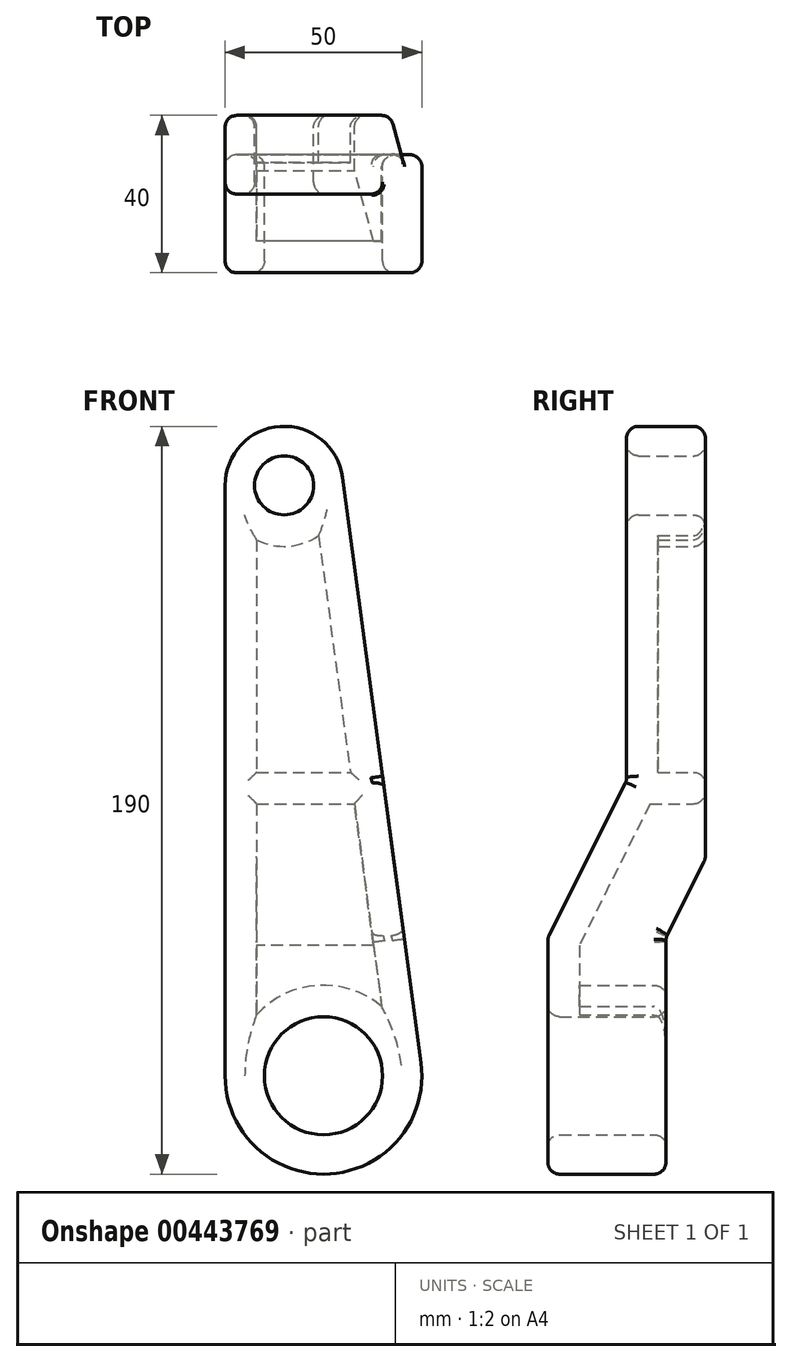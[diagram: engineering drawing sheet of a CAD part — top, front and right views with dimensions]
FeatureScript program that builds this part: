
annotation { "Feature Type Name" : "Feature", "Feature Type Description" : "" }
export const myFeature = defineFeature(function(context is Context, id is Id, definition is map)
    precondition{}
    {
        {
            var Q0;
            Q0=qCreatedBy(makeId("Front.planeOp"),FACE);
            var sketch = newSketch(context, id + "F0", { "sketchPlane" : qUnion([Q0])});
            skArc(sketch, "E0", {"start": v(-25, 0) * mm, "mid": v(1.66, -24.94) * mm, "end": v(24.78, 3.32) * mm});
            skArc(sketch, "E1", {"start": v(4.87, 152) * mm, "mid": v(-11, 164.97) * mm, "end": v(-25, 150) * mm});
            skLineSegment(sketch, "E2", {"start": v(-25, 150) * mm, "end": v(-25, 0) * mm});
            skLineSegment(sketch, "E3", {"start": v(4.87, 152) * mm, "end": v(24.78, 3.32) * mm});
            skPoint(sketch, "E4.orphan", {"position": v(0, 188.33) * mm});
            skSolve(sketch);
        }
        {
            var Q0;
            Q0=makeQuery(id+"F0.imprint","IMPRINT",FACE,{"disambiguationData":[TD([[makeQuery(id+"F0.imprint","IMPRINT",EDGE,{"derivedFrom":sQuery(id+"F0.wireOp",EDGE,"E0")}),1.0]])]});
            extrude(context, id + "F1", {"entities" : qUnion([Q0]), "depth" : 40 * mm});
        }
        {
            var Q0;
            Q0=makeQuery(id+"F1.opExtrude","SWEPT_FACE",FACE,{"disambiguationData":[OSD([sQuery(id+"F0.wireOp",EDGE,"E2")])]});
            var sketch = newSketch(context, id + "F2", { "sketchPlane" : qUnion([Q0])});
            skPoint(sketch, "E5.endSnap0", {"position": v(20, 0) * mm});
            skLineSegment(sketch, "E6", {"start": v(0, 55) * mm, "end": v(0, -25.94) * mm});
            skLineSegment(sketch, "E7", {"start": v(10, -25.94) * mm, "end": v(10, 35) * mm});
            skLineSegment(sketch, "E8", {"start": v(10, 35) * mm, "end": v(0, 55) * mm});
            skLineSegment(sketch, "E9", {"start": v(40, 35) * mm, "end": v(40, 165.97) * mm});
            skLineSegment(sketch, "E10", {"start": v(20, 165.97) * mm, "end": v(20, 75) * mm});
            skLineSegment(sketch, "E11", {"start": v(20, 75) * mm, "end": v(40, 35) * mm});
            skLineSegment(sketch, "E12", {"start": v(0, -25.94) * mm, "end": v(10, -25.94) * mm});
            skLineSegment(sketch, "E13", {"start": v(20, 165.97) * mm, "end": v(40, 165.97) * mm});
            skSolve(sketch);
        }
        {
            var Q0;
            Q0 = qSketchRegion(id + "F2", true);
            extrude(context, id + "F3", {"entities" : qUnion([Q0]), "operationType" : NewBodyOperationType.REMOVE, "endBound" : BoundingType.THROUGH_ALL, "oppositeDirection" : true, "depth" : 25 * mm});
        }
        {
            var Q0;
            Q0=makeQuery(id+"F1.opExtrude","CAP_FACE",FACE,{"disambiguationData":[OSD([sQuery(id+"F0.wireOp",EDGE,"E0"),sQuery(id+"F0.wireOp",EDGE,"E1"),sQuery(id+"F0.wireOp",EDGE,"E2"),sQuery(id+"F0.wireOp",EDGE,"E3")])],"isStart":true});
            var sketch = newSketch(context, id + "F4", { "sketchPlane" : qUnion([Q0])});
            skCircle(sketch, "E14", {"center": v(10, 150) * mm, "radius": 7.5 * mm});
            skCircle(sketch, "E15", {"center": v(0, 0) * mm, "radius": 15 * mm});
            skSolve(sketch);
        }
        {
            var Q0;
            Q0 = qSketchRegion(id + "F4", true);
            extrude(context, id + "F5", {"entities" : qUnion([Q0]), "operationType" : NewBodyOperationType.REMOVE, "endBound" : BoundingType.THROUGH_ALL, "oppositeDirection" : true, "depth" : 25 * mm});
        }
        {
            var Q0;
            Q0=makeQuery(id+"F1.opExtrude","CAP_FACE",FACE,{"disambiguationData":[OSD([sQuery(id+"F0.wireOp",EDGE,"E0"),sQuery(id+"F0.wireOp",EDGE,"E1"),sQuery(id+"F0.wireOp",EDGE,"E2"),sQuery(id+"F0.wireOp",EDGE,"E3")])],"isStart":true});
            var Q1;
            Q1=makeQuery(id+"F3.boolean.opBoolean","COPY",FACE,{"derivedFrom":makeQuery(id+"F3.opExtrude","SWEPT_FACE",FACE,{"disambiguationData":[OSD([sQuery(id+"F2.wireOp",EDGE,"E8")])]})});
            var Q2;
            Q2=makeQuery(id+"F3.boolean.opBoolean","COPY",FACE,{"derivedFrom":makeQuery(id+"F3.opExtrude","SWEPT_FACE",FACE,{"disambiguationData":[OSD([sQuery(id+"F2.wireOp",EDGE,"E7")])]})});
            shell(context, id + "F6", {"entities" : qUnion([Q0, Q1, Q2]), "thickness" : 8 * mm});
        }
        {
            var Q0;
            Q0=makeQuery(id+"F1.opExtrude","CAP_FACE",FACE,{"disambiguationData":[OSD([sQuery(id+"F0.wireOp",EDGE,"E0"),sQuery(id+"F0.wireOp",EDGE,"E1"),sQuery(id+"F0.wireOp",EDGE,"E2"),sQuery(id+"F0.wireOp",EDGE,"E3")])],"isStart":true});
            var sketch = newSketch(context, id + "F7", { "sketchPlane" : qUnion([Q0])});
            skLineSegment(sketch, "E16", {"start": v(-6.82, 77.11) * mm, "end": v(17, 77.11) * mm});
            skLineSegment(sketch, "E17", {"start": v(-7.9, 69.11) * mm, "end": v(17, 69.11) * mm});
            skLineSegment(sketch, "E18.0", {"start": v(-6.82, 77.11) * mm, "end": v(-7.9, 69.11) * mm});
            skLineSegment(sketch, "E19.0", {"start": v(17, 77.11) * mm, "end": v(17, 69.11) * mm});
            skPoint(sketch, "E20.orphan", {"position": v(1.23, 137.22) * mm});
            skPoint(sketch, "E21.orphan", {"position": v(17, 136.17) * mm});
            skPoint(sketch, "E22.orphan", {"position": v(17, 55) * mm});
            skPoint(sketch, "E23.orphan", {"position": v(-9.79, 55) * mm});
            skSolve(sketch);
        }
        {
            var Q0;
            Q0 = qSketchRegion(id + "F7", true);
            extrude(context, id + "F8", {"entities" : qUnion([Q0]), "operationType" : NewBodyOperationType.ADD, "endBound" : BoundingType.UP_TO_NEXT, "oppositeDirection" : true, "depth" : 25 * mm});
        }
        {
            var Q0;
            Q0=makeQuery(id+"F1.opExtrude","CAP_EDGE",EDGE,{"disambiguationData":[OSD([sQuery(id+"F0.wireOp",EDGE,"E1")])],"isStart":true});
            var Q1;
            Q1=makeQuery(id+"F8.boolean.opBoolean","MERGE",FACE,{"derivedFrom":[makeQuery(id+"F1.opExtrude","CAP_FACE",FACE,{"disambiguationData":[OSD([sQuery(id+"F0.wireOp",EDGE,"E0"),sQuery(id+"F0.wireOp",EDGE,"E1"),sQuery(id+"F0.wireOp",EDGE,"E2"),sQuery(id+"F0.wireOp",EDGE,"E3")])],"isStart":true}),makeQuery(id+"F8.opExtrude","CAP_FACE",FACE,{"disambiguationData":[OSD([sQuery(id+"F7.wireOp",EDGE,"E16"),sQuery(id+"F7.wireOp",EDGE,"E17"),sQuery(id+"F7.wireOp",EDGE,"E18.0"),sQuery(id+"F7.wireOp",EDGE,"E19.0")])],"isStart":true})]});
            var Q2;
            Q2=makeQuery(id+"F3.boolean.opBoolean","INTERSECT",EDGE,{"derivedFrom":[makeQuery(id+"F1.opExtrude","SWEPT_FACE",FACE,{"disambiguationData":[OSD([sQuery(id+"F0.wireOp",EDGE,"E3")])]}),makeQuery(id+"F3.opExtrude","SWEPT_FACE",FACE,{"disambiguationData":[OSD([sQuery(id+"F2.wireOp",EDGE,"E10")])]})]});
            var Q3;
            Q3=makeQuery(id+"F3.boolean.opBoolean","INTERSECT",EDGE,{"derivedFrom":[makeQuery(id+"F1.opExtrude","SWEPT_FACE",FACE,{"disambiguationData":[OSD([sQuery(id+"F0.wireOp",EDGE,"E3")])]}),makeQuery(id+"F3.opExtrude","SWEPT_FACE",FACE,{"disambiguationData":[OSD([sQuery(id+"F2.wireOp",EDGE,"E11")])]})]});
            var Q4;
            Q4=makeQuery(id+"F3.boolean.opBoolean","INTERSECT",EDGE,{"derivedFrom":[makeQuery(id+"F1.opExtrude","SWEPT_FACE",FACE,{"disambiguationData":[OSD([sQuery(id+"F0.wireOp",EDGE,"E3")])]}),makeQuery(id+"F3.opExtrude","SWEPT_FACE",FACE,{"disambiguationData":[OSD([sQuery(id+"F2.wireOp",EDGE,"E7")])]})]});
            var Q5;
            Q5=makeQuery(id+"F3.boolean.opBoolean","INTERSECT",EDGE,{"derivedFrom":[makeQuery(id+"F1.opExtrude","SWEPT_FACE",FACE,{"disambiguationData":[OSD([sQuery(id+"F0.wireOp",EDGE,"E3")])]}),makeQuery(id+"F3.opExtrude","SWEPT_FACE",FACE,{"disambiguationData":[OSD([sQuery(id+"F2.wireOp",EDGE,"E8")])]})]});
            var Q6;
            Q6=makeQuery(id+"F1.opExtrude","CAP_EDGE",EDGE,{"disambiguationData":[OSD([sQuery(id+"F0.wireOp",EDGE,"E3")])],"isStart":false});
            var Q7;
            Q7=makeQuery(id+"F3.boolean.opBoolean","INTERSECT",EDGE,{"derivedFrom":[makeQuery(id+"F1.opExtrude","SWEPT_FACE",FACE,{"disambiguationData":[OSD([sQuery(id+"F0.wireOp",EDGE,"E0")])]}),makeQuery(id+"F3.opExtrude","SWEPT_FACE",FACE,{"disambiguationData":[OSD([sQuery(id+"F2.wireOp",EDGE,"E7")])]})]});
            var Q8;
            Q8=makeQuery(id+"F1.opExtrude","CAP_EDGE",EDGE,{"disambiguationData":[OSD([sQuery(id+"F0.wireOp",EDGE,"E0")])],"isStart":false});
            var Q9;
            Q9=makeQuery(id+"F3.boolean.opBoolean","COPY",FACE,{"derivedFrom":makeQuery(id+"F3.opExtrude","SWEPT_FACE",FACE,{"disambiguationData":[OSD([sQuery(id+"F2.wireOp",EDGE,"E7")])]})});
            var Q10;
            Q10=makeQuery(id+"F3.boolean.opBoolean","COPY",FACE,{"derivedFrom":makeQuery(id+"F3.opExtrude","SWEPT_FACE",FACE,{"disambiguationData":[OSD([sQuery(id+"F2.wireOp",EDGE,"E8")])]})});
            var Q11;
            Q11=makeQuery(id+"F6.opShell","OFFSET_EDGE",EDGE,{"disambiguationData":[OSD([sQuery(id+"F0.wireOp",EDGE,"E3"),sQuery(id+"F2.wireOp",EDGE,"E8")])]});
            var Q12;
            Q12=makeQuery(id+"F1.opExtrude","SWEPT_FACE",FACE,{"disambiguationData":[OSD([sQuery(id+"F0.wireOp",EDGE,"E1")])]});
            var Q13;
            Q13=makeQuery(id+"F3.boolean.opBoolean","COPY",FACE,{"derivedFrom":makeQuery(id+"F3.opExtrude","SWEPT_FACE",FACE,{"disambiguationData":[OSD([sQuery(id+"F2.wireOp",EDGE,"E11")])]})});
            var Q14;
            Q14=makeQuery(id+"F1.opExtrude","CAP_EDGE",EDGE,{"disambiguationData":[OSD([sQuery(id+"F0.wireOp",EDGE,"E2")])],"isStart":false});
            var Q15;
            Q15=makeQuery(id+"F3.boolean.opBoolean","COPY",FACE,{"derivedFrom":makeQuery(id+"F3.opExtrude","SWEPT_FACE",FACE,{"disambiguationData":[OSD([sQuery(id+"F2.wireOp",EDGE,"E10")])]})});
            var Q16;
            Q16=makeQuery(id+"F5.boolean.opBoolean","INTERSECT",EDGE,{"derivedFrom":[makeQuery(id+"F1.opExtrude","CAP_FACE",FACE,{"disambiguationData":[OSD([sQuery(id+"F0.wireOp",EDGE,"E0"),sQuery(id+"F0.wireOp",EDGE,"E1"),sQuery(id+"F0.wireOp",EDGE,"E2"),sQuery(id+"F0.wireOp",EDGE,"E3")])],"isStart":false}),makeQuery(id+"F5.opExtrude","SWEPT_FACE",FACE,{"disambiguationData":[OSD([sQuery(id+"F4.wireOp",EDGE,"E15")])]})]});
            fillet(context, id + "F9", {"entities" : qUnion([Q0, Q1, Q2, Q3, Q4, Q5, Q6, Q7, Q8, Q9, Q10, Q11, Q12, Q13, Q14, Q15, Q16]), "radius" : 3 * mm, "tangentPropagation" : true, "allowEdgeOverflow" : false});
        }
    });
